# Revit family: BOX BD
name_source: partatom
category: Modelos genéricos
revit_build: Autodesk Revit 2017 (Build: 20160225_1515(x64)
units: mm (PartAtom-declared; Revit-internal decimal feet)

## family parameters
Compartido = No
Corte con vacíos al cargar = No
Cota de conector redondo = Diámetro de uso
Puede alojar armadura = No
Punto de cálculo de habitación = No
Se basa en plano de trabajo = No
Siempre vertical = Sí
Tipo de pieza = Normal

## types (5) — shared parameters
Esp = 3 mm  [stored 0.00984252 ft]
Fabricante = Casals Ventilación
M = 23 mm  [stored 0.0754593 ft]
Material = <Por categoría>
N = 27 mm  [stored 0.0885827 ft]
URL = www.casals.com

## per-type parameters (varying)
| type | A | B | C | D | Dimensiones | E | F | H | I | J | K | L |
| BOX BD 7/7 | 450 mm  [stored 1.47638 ft] | 450 mm  [stored 1.47638 ft] | 450 mm  [stored 1.47638 ft] | 252 mm  [stored 0.826772 ft] | 450x450x500 | 229 mm | 76 mm  [stored 0.249344 ft] | 145 mm  [stored 0.475722 ft] | 352 mm  [stored 1.15486 ft] | 312 mm  [stored 1.02362 ft] | 60 mm  [stored 0.19685 ft] | 78 mm  [stored 0.255906 ft] |
| BOX BD 9/9 | 535 mm  [stored 1.75525 ft] | 535 mm  [stored 1.75525 ft] | 535 mm  [stored 1.75525 ft] | 321 mm  [stored 1.05315 ft] | 535x535x585 | 280 mm | 91 mm  [stored 0.298556 ft] | 164 mm  [stored 0.538058 ft] | 418 mm  [stored 1.37139 ft] | 361 mm  [stored 1.18438 ft] | 78 mm  [stored 0.255906 ft] | 96 mm  [stored 0.314961 ft] |
| BOX BD 10/10 | 580 mm  [stored 1.90289 ft] | 580 mm  [stored 1.90289 ft] | 580 mm  [stored 1.90289 ft] | 352 mm  [stored 1.15486 ft] | 580x580x630
580x580x630 | 311 mm | 79 mm | 190 mm | 493 mm  [stored 1.61745 ft] | 423 mm  [stored 1.3878 ft] | 69 mm  [stored 0.226378 ft] | 88 mm  [stored 0.288714 ft] |
| BOX BD 12/12 | 650 mm  [stored 2.13255 ft] | 650 mm  [stored 2.13255 ft] | 650 mm  [stored 2.13255 ft] | 418 mm  [stored 1.37139 ft] | 650x650x700 | 361 mm  [stored 1.18438 ft] | 78 mm  [stored 0.255906 ft] | 211 mm  [stored 0.692257 ft] | 576 mm  [stored 1.88976 ft] | 502 mm | 65 mm  [stored 0.213255 ft] | 83 mm  [stored 0.27231 ft] |
| BOX BD 15/15 | 775 mm  [stored 2.54265 ft] | 775 mm  [stored 2.54265 ft] | 775 mm  [stored 2.54265 ft] | 493 mm  [stored 1.61745 ft] | 775x775x825 | 423 mm  [stored 1.3878 ft] | 113 mm  [stored 0.370735 ft] | 239 mm  [stored 0.784121 ft] | 650 mm  [stored 2.13255 ft] | 652 mm | 52 mm | 71 mm  [stored 0.23294 ft] |

note: [stored X ft] marks values corroborated as IEEE doubles in the binary element streams (Revit-internal decimal feet)
